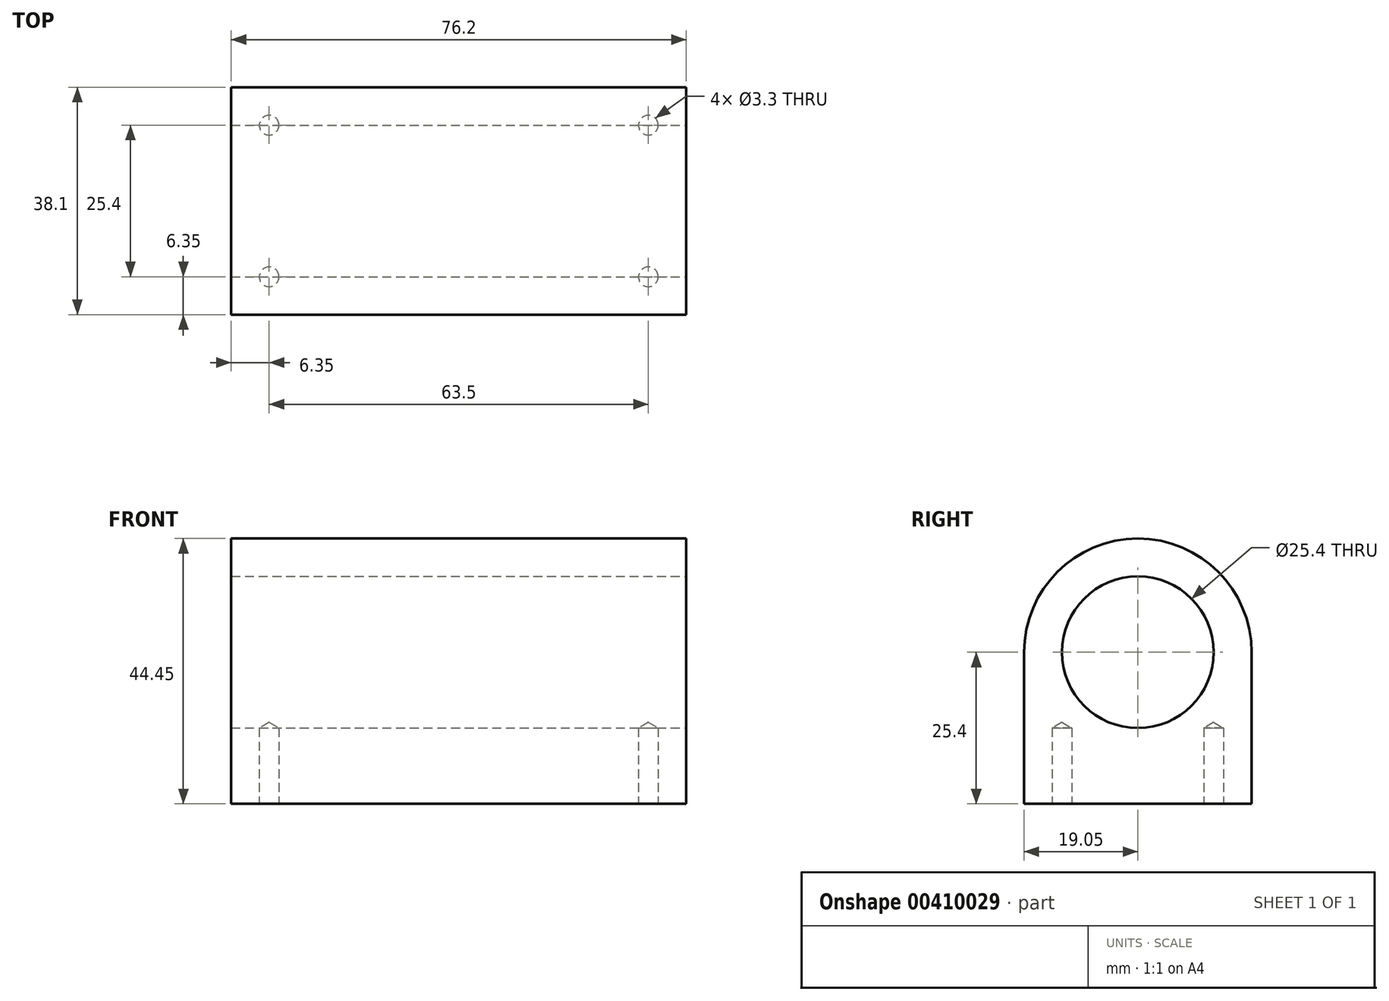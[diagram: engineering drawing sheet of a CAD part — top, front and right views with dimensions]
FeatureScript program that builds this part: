
annotation { "Feature Type Name" : "Feature", "Feature Type Description" : "" }
export const myFeature = defineFeature(function(context is Context, id is Id, definition is map)
    precondition{}
    {
        {
            var Q0;
            Q0=qCreatedBy(makeId("Right.planeOp"),FACE);
            var sketch = newSketch(context, id + "F0", { "sketchPlane" : qUnion([Q0])});
            skLineSegment(sketch, "E0.bottom", {"start": v(19.05, 0) * mm, "end": v(-19.05, 0) * mm});
            skLineSegment(sketch, "E0.top", {"start": v(19.05, -25.4) * mm, "end": v(-19.05, -25.4) * mm});
            skLineSegment(sketch, "E0.left", {"start": v(19.05, 0) * mm, "end": v(19.05, -25.4) * mm});
            skLineSegment(sketch, "E0.right", {"start": v(-19.05, 0) * mm, "end": v(-19.05, -25.4) * mm});
            skPoint(sketch, "E0.middle", {"position": v(0, -12.7) * mm});
            skCircle(sketch, "E1", {"center": v(0, 0) * mm, "radius": 19.05 * mm});
            skSolve(sketch);
        }
        {
            var Q0;
            Q0 = qSketchRegion(id + "F0", true);
            extrude(context, id + "F1", {"entities" : qUnion([Q0]), "depth" : 76.2 * mm});
        }
        {
            var Q0;
            Q0=makeQuery(id+"F1.opExtrude","SWEPT_FACE",FACE,{"disambiguationData":[OSD([sQuery(id+"F0.wireOp",EDGE,"E0.top")])]});
            var sketch = newSketch(context, id + "F2", { "sketchPlane" : qUnion([Q0])});
            skCircle(sketch, "E2", {"center": v(6.35, 12.7) * mm, "radius": 1.65 * mm});
            skCircle(sketch, "E3", {"center": v(6.35, -12.7) * mm, "radius": 1.65 * mm});
            skCircle(sketch, "E4", {"center": v(69.85, 12.7) * mm, "radius": 1.65 * mm});
            skCircle(sketch, "E5", {"center": v(69.85, -12.7) * mm, "radius": 1.65 * mm});
            skSolve(sketch);
        }
        {
            var Q0;
            Q0=sQuery(id+"F2.wireOp",VERTEX,"E2.center");
            var Q1;
            Q1=sQuery(id+"F2.wireOp",VERTEX,"E3.center");
            var Q2;
            Q2=sQuery(id+"F2.wireOp",VERTEX,"E5.center");
            var Q3;
            Q3=sQuery(id+"F2.wireOp",VERTEX,"E4.center");
            var Q4;
            Q4=makeQuery(id+"F1.opExtrude","SWEPT_BODY",BODY,{"disambiguationData":[OSD([sQuery(id+"F0.wireOp",EDGE,"E0.top"),sQuery(id+"F0.wireOp",EDGE,"E0.left"),sQuery(id+"F0.wireOp",EDGE,"E0.right"),sQuery(id+"F0.wireOp",EDGE,"E1")])]});
            hole(context, id + "F3", {"style" : HoleStyle.SIMPLE, "endStyle" : HoleEndStyle.BLIND, "holeDiameter" : 3.3 * mm, "holeDepth" : 12.7 * mm, "isTappedThrough" : true, "tappedDepth" : 12.7 * mm, "tapClearance" : 3, "locations" : qUnion([Q0, Q1, Q2, Q3]), "scope" : qUnion([Q4])});
        }
        {
            var Q0;
            Q0=makeQuery(id+"F1.opExtrude","CAP_FACE",FACE,{"disambiguationData":[OSD([sQuery(id+"F0.wireOp",EDGE,"E0.top"),sQuery(id+"F0.wireOp",EDGE,"E0.left"),sQuery(id+"F0.wireOp",EDGE,"E0.right"),sQuery(id+"F0.wireOp",EDGE,"E1")])],"isStart":false});
            var sketch = newSketch(context, id + "F4", { "sketchPlane" : qUnion([Q0])});
            skCircle(sketch, "E6", {"center": v(0, 0) * mm, "radius": 12.7 * mm});
            skSolve(sketch);
        }
        {
            var Q0;
            Q0=makeQuery(id+"F4.imprint","IMPRINT",FACE,{"disambiguationData":[TD([[makeQuery(id+"F4.imprint","IMPRINT",EDGE,{"derivedFrom":sQuery(id+"F4.wireOp",EDGE,"E6")}),1.0]])]});
            extrude(context, id + "F5", {"entities" : qUnion([Q0]), "operationType" : NewBodyOperationType.REMOVE, "endBound" : BoundingType.THROUGH_ALL, "oppositeDirection" : true, "depth" : 25.4 * mm});
        }
    });
